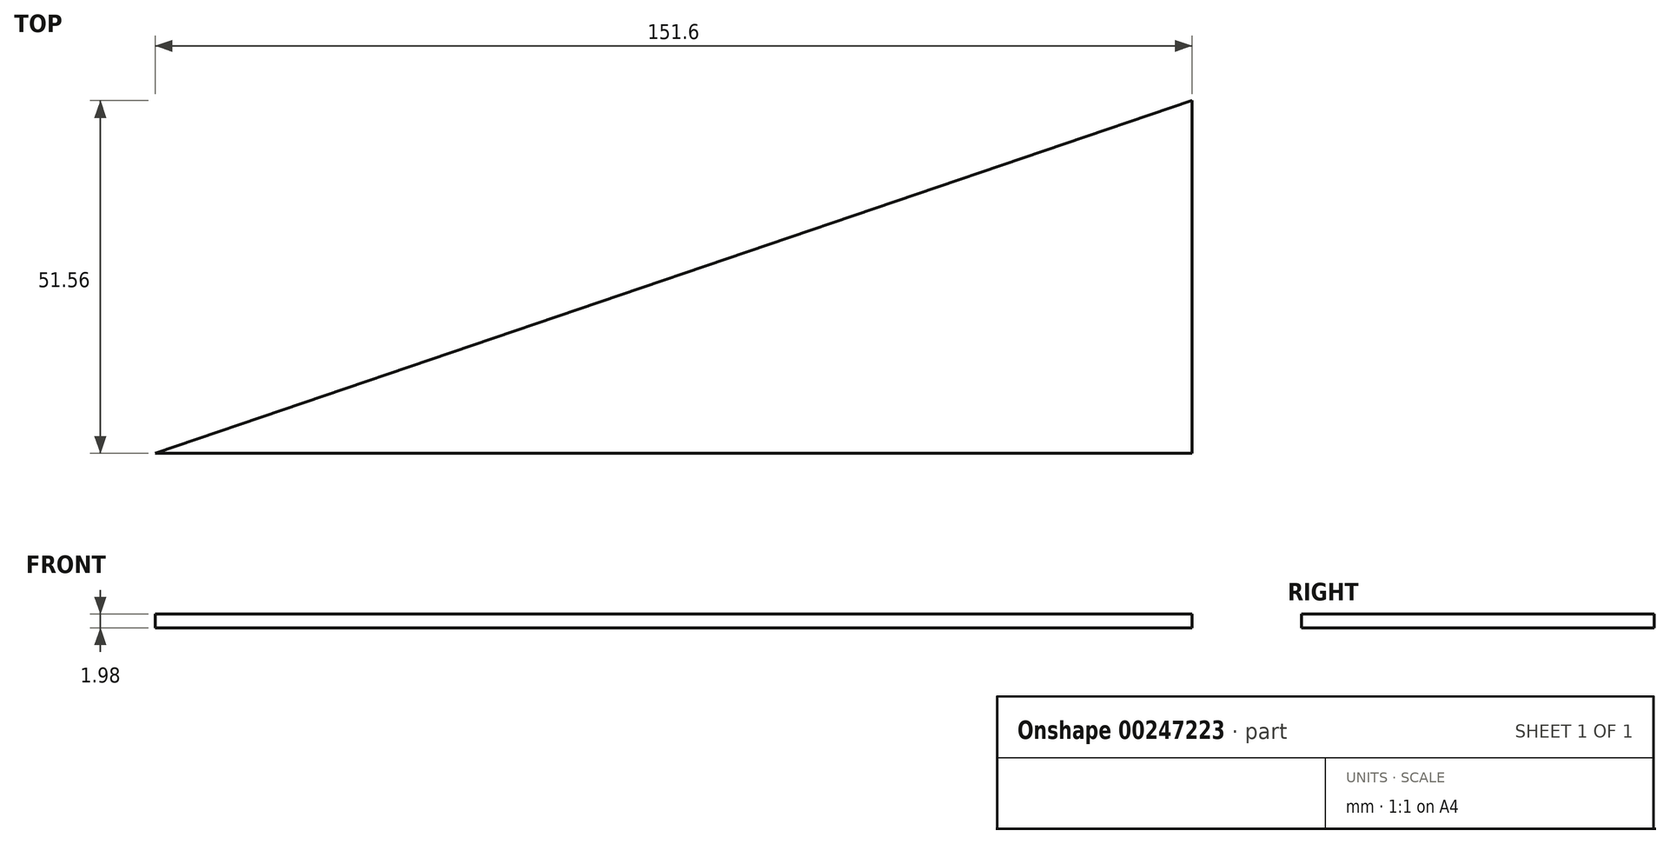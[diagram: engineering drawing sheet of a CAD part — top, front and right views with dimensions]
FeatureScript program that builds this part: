
annotation { "Feature Type Name" : "Feature", "Feature Type Description" : "" }
export const myFeature = defineFeature(function(context is Context, id is Id, definition is map)
    precondition{}
    {
        {
            var Q0;
            Q0=qCreatedBy(makeId("Top.planeOp"),FACE);
            var sketch = newSketch(context, id + "F0", { "sketchPlane" : qUnion([Q0])});
            skLineSegment(sketch, "E0", {"start": v(-76.57, 0) * mm, "end": v(75.03, 0) * mm});
            skLineSegment(sketch, "E1", {"start": v(75.03, 0) * mm, "end": v(75.03, 51.56) * mm});
            skLineSegment(sketch, "E2", {"start": v(75.03, 51.56) * mm, "end": v(-76.57, 0) * mm});
            skSolve(sketch);
        }
        {
            var Q0;
            Q0 = qSketchRegion(id + "F0", true);
            extrude(context, id + "F1", {"entities" : qUnion([Q0]), "depth" : 1.98 * mm});
        }
    });
